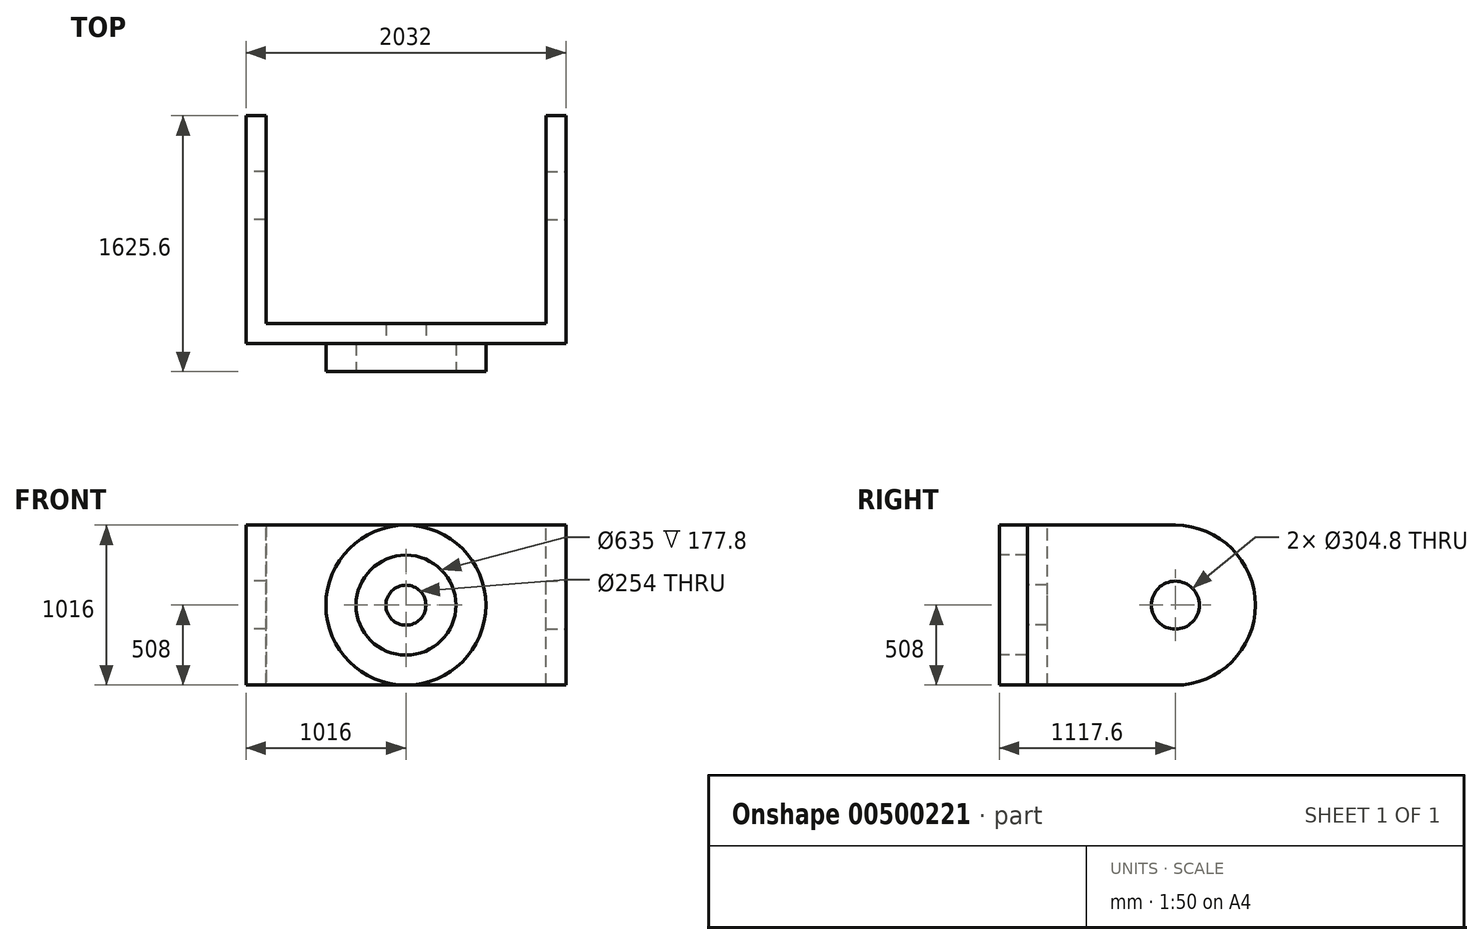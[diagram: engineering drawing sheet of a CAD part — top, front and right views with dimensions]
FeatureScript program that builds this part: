
annotation { "Feature Type Name" : "Feature", "Feature Type Description" : "" }
export const myFeature = defineFeature(function(context is Context, id is Id, definition is map)
    precondition{}
    {
        {
            var Q0;
            Q0=qCreatedBy(makeId("Front.planeOp"),FACE);
            var sketch = newSketch(context, id + "F0", { "sketchPlane" : qUnion([Q0])});
            skCircle(sketch, "E0", {"center": v(0, 0) * mm, "radius": 127 * mm});
            skCircle(sketch, "E1", {"center": v(0, 0) * mm, "radius": 317.5 * mm});
            skCircle(sketch, "E2", {"center": v(0, 0) * mm, "radius": 508 * mm});
            skLineSegment(sketch, "E3.bottom", {"start": v(1016, -508) * mm, "end": v(-1016, -508) * mm});
            skLineSegment(sketch, "E3.top", {"start": v(1016, 508) * mm, "end": v(-1016, 508) * mm});
            skLineSegment(sketch, "E3.left", {"start": v(1016, -508) * mm, "end": v(1016, 508) * mm});
            skLineSegment(sketch, "E3.right", {"start": v(-1016, -508) * mm, "end": v(-1016, 508) * mm});
            skSolve(sketch);
        }
        {
            var Q0;
            {var subQ5=sQuery(id+"F0.wireOp",EDGE,"E3.left");Q0=makeQuery(id+"F0.imprint","IMPRINT",FACE,{"disambiguationData":[TD([[makeQuery(id+"F0.imprint","IMPRINT",EDGE,{"derivedFrom":subQ5}),1.0]])]});}
            var Q1;
            {var subQ5=sQuery(id+"F0.wireOp",EDGE,"E3.right");Q1=makeQuery(id+"F0.imprint","IMPRINT",FACE,{"disambiguationData":[TD([[makeQuery(id+"F0.imprint","IMPRINT",EDGE,{"derivedFrom":subQ5}),-1.0]])]});}
            var Q2;
            Q2=makeQuery(id+"F0.imprint","IMPRINT",FACE,{"disambiguationData":[TD([[makeQuery(id+"F0.imprint","IMPRINT",EDGE,{"derivedFrom":sQuery(id+"F0.wireOp",EDGE,"E1")}),-1.0]])]});
            extrude(context, id + "F1", {"entities" : qUnion([Q0, Q1, Q2]), "oppositeDirection" : true, "depth" : 127 * mm});
        }
        {
            var Q0;
            Q0=makeQuery(id+"F0.imprint","IMPRINT",FACE,{"disambiguationData":[TD([[makeQuery(id+"F0.imprint","IMPRINT",EDGE,{"derivedFrom":sQuery(id+"F0.wireOp",EDGE,"E1")}),-1.0]])]});
            extrude(context, id + "F2", {"entities" : qUnion([Q0]), "operationType" : NewBodyOperationType.ADD, "depth" : 177.8 * mm});
        }
        {
            var Q0;
            Q0=makeQuery(id+"F0.imprint","IMPRINT",FACE,{"disambiguationData":[TD([[makeQuery(id+"F0.imprint","IMPRINT",EDGE,{"derivedFrom":sQuery(id+"F0.wireOp",EDGE,"E0")}),-1.0]])]});
            extrude(context, id + "F3", {"entities" : qUnion([Q0]), "operationType" : NewBodyOperationType.ADD, "oppositeDirection" : true, "depth" : 127 * mm});
        }
        {
            var Q0;
            Q0=makeQuery(id+"F1.opExtrude","SWEPT_FACE",FACE,{"disambiguationData":[OSD([sQuery(id+"F0.wireOp",EDGE,"E3.right")])]});
            var sketch = newSketch(context, id + "F4", { "sketchPlane" : qUnion([Q0])});
            skLineSegment(sketch, "E4", {"start": v(0, 508) * mm, "end": v(-939.8, 508) * mm});
            skLineSegment(sketch, "E5", {"start": v(-939.8, -508) * mm, "end": v(0, -508) * mm});
            skCircle(sketch, "E6", {"center": v(-939.8, 0) * mm, "radius": 152.4 * mm});
            skArc(sketch, "E7", {"start": v(-939.8, 508) * mm, "mid": v(-1447.8, 0) * mm, "end": v(-939.8, -508) * mm});
            skSolve(sketch);
        }
        {
            var Q0;
            Q0=makeQuery(id+"F4.imprint","IMPRINT",FACE,{"disambiguationData":[TD([[makeQuery(id+"F4.imprint","IMPRINT",EDGE,{"derivedFrom":sQuery(id+"F4.wireOp",EDGE,"E6")}),-1.0]])]});
            extrude(context, id + "F5", {"entities" : qUnion([Q0]), "operationType" : NewBodyOperationType.ADD, "oppositeDirection" : true, "depth" : 127 * mm});
        }
        {
            var Q0;
            Q0=makeQuery(id+"F1.opExtrude","SWEPT_FACE",FACE,{"disambiguationData":[OSD([sQuery(id+"F0.wireOp",EDGE,"E3.left")])]});
            var sketch = newSketch(context, id + "F6", { "sketchPlane" : qUnion([Q0])});
            skLineSegment(sketch, "E8", {"start": v(0, -508) * mm, "end": v(939.8, -508) * mm});
            skLineSegment(sketch, "E9", {"start": v(939.8, 508) * mm, "end": v(0, 508) * mm});
            skArc(sketch, "E10", {"start": v(939.8, -508) * mm, "mid": v(1447.8, 0) * mm, "end": v(939.8, 508) * mm});
            skCircle(sketch, "E11", {"center": v(939.8, 0) * mm, "radius": 152.4 * mm});
            skSolve(sketch);
        }
        {
            var Q0;
            {var subQ0=sQuery(id+"F6.wireOp",EDGE,"E10");Q0=makeQuery(id+"F6.imprint","IMPRINT",FACE,{"disambiguationData":[TD([[makeQuery(id+"F6.imprint","IMPRINT",EDGE,{"derivedFrom":subQ0}),1.0]])]});}
            extrude(context, id + "F7", {"entities" : qUnion([Q0]), "operationType" : NewBodyOperationType.ADD, "oppositeDirection" : true, "depth" : 127 * mm});
        }
    });
